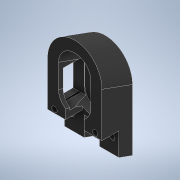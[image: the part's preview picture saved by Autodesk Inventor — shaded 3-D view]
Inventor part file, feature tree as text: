
AUTODESK INVENTOR PART (.ipt)
format: ipt  version: 2021 (Build 250183000, 183)  size: 254,464 bytes
history: native  units: mm
features: sketch x6, extrude x5, sweep x2, fillet x1
ambient origin geometry x8: Origin, YZ Plane, XZ Plane, XY Plane, X Axis, Y Axis, Z Axis, Center Point
bodies: Solid1 (feature_tree)
feature tree (14):
  sketch  "Sketch1"  dims[d0=32.0mm d1=37.209mm]
  sketch  "Sketch2"  dims[d2=13.834mm d3=19.0mm]
  sweep  "Sweep1"
  sweep  "Sweep2"
  extrude  "Extrusion1"  Depth=12.0mm
  extrude  "Extrusion2"  Depth=12.217305mm
  extrude  "Extrusion3"  Depth=18.0mm
  fillet  "Fillet1"  [1 undecoded]
  sketch  "Sketch5"  dims[d11=0.0mm d12=0.0mm d13=18.0mm d15=0.0mm d16=0.0mm]
  extrude  "Extrusion6"  Depth=10.0mm TaperAngle=0.0deg
  extrude  "Extrusion7"  Depth=10.0mm
  sketch  "Sketch3"  dims[d5=12.0mm d6=12.0mm]
  sketch  "Sketch4"  dims[d8=3.2mm d9=12.217305mm]
  sketch  "Sketch6"  dims[d17=7.0mm d18=10.0mm d19=0.0mm d20=12.3mm d21=19.5mm d23=20.0mm d24=16.25mm d25=0.0mm d26=10.0mm d27=4.0mm d28=13.875mm d29=0.0mm d30=0.0mm d31=2.5mm d32=16.0mm d33=3.0mm d34=37.0mm d35=11.493mm d36=10.0mm d37=6.0mm d38=11.0mm d39=11.5mm d40=1.5mm d41=9.0mm d42=1.8mm d43=5.0mm d48=7.0mm d49=9.0mm d50=5.25mm d51=0.0mm d52=7.0mm d53=10.0mm d54=5.0mm d55=15.0mm d56=0.0mm d14=0.872665mm]
note: 1 required parameter value undecoded (feature->parameter linkage not recoverable at this tier; creation-order binding heuristic only, values carry confidence <= 0.55)
